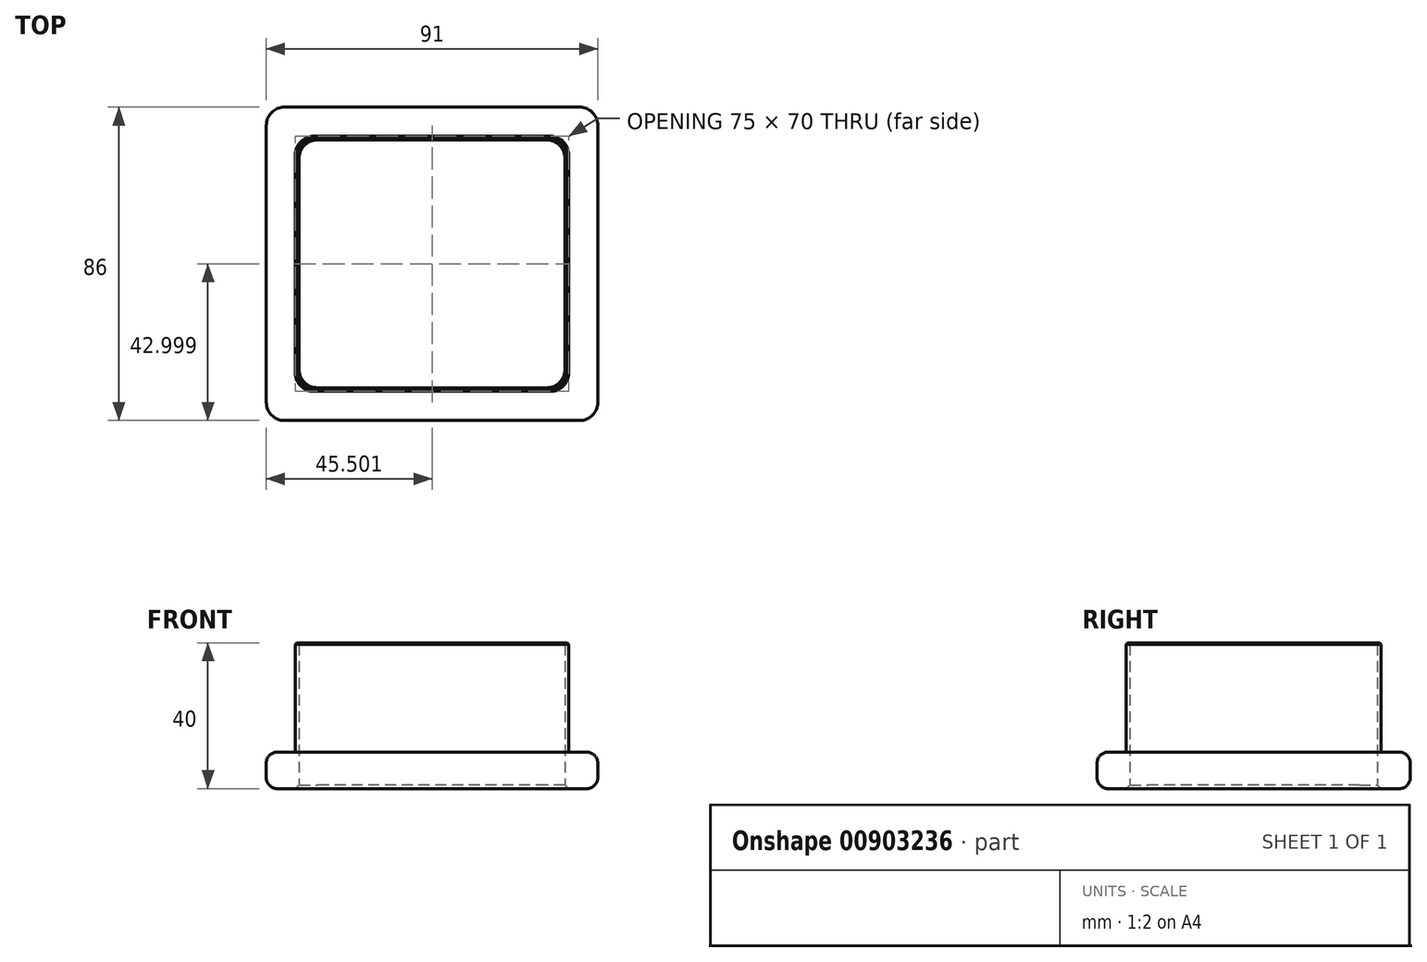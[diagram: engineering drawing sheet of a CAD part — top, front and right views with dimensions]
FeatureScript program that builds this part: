
annotation { "Feature Type Name" : "Feature", "Feature Type Description" : "" }
export const myFeature = defineFeature(function(context is Context, id is Id, definition is map)
    precondition{}
    {
        {
            var Q0;
            Q0=qCreatedBy(makeId("Top.planeOp"),FACE);
            var sketch = newSketch(context, id + "F0", { "sketchPlane" : qUnion([Q0])});
            skLineSegment(sketch, "E0.bottom", {"start": v(-97.4, 29.69) * mm, "end": v(-32.4, 29.69) * mm});
            skLineSegment(sketch, "E0.top", {"start": v(-97.4, -40.31) * mm, "end": v(-32.4, -40.31) * mm});
            skLineSegment(sketch, "E0.left", {"start": v(-102.4, 24.69) * mm, "end": v(-102.4, -35.31) * mm});
            skLineSegment(sketch, "E0.right", {"start": v(-27.4, 24.69) * mm, "end": v(-27.4, -35.31) * mm});
            skLineSegment(sketch, "E1.0", {"start": v(-101.4, 23.69) * mm, "end": v(-101.4, -34.31) * mm});
            skLineSegment(sketch, "E1.1", {"start": v(-96.4, 28.69) * mm, "end": v(-33.4, 28.69) * mm});
            skLineSegment(sketch, "E1.2", {"start": v(-28.4, 23.69) * mm, "end": v(-28.4, -34.31) * mm});
            skLineSegment(sketch, "E1.3", {"start": v(-96.4, -39.31) * mm, "end": v(-33.4, -39.31) * mm});
            skLineSegment(sketch, "E2.0", {"start": v(-105.4, 27.69) * mm, "end": v(-105.4, -38.31) * mm});
            skLineSegment(sketch, "E2.1", {"start": v(-100.4, 32.69) * mm, "end": v(-29.4, 32.69) * mm});
            skLineSegment(sketch, "E2.2", {"start": v(-24.4, 27.69) * mm, "end": v(-24.4, -38.31) * mm});
            skLineSegment(sketch, "E2.3", {"start": v(-100.4, -43.31) * mm, "end": v(-29.4, -43.31) * mm});
            skPoint(sketch, "E3.visualSharp", {"position": v(-101.4, 28.69) * mm});
            skArc(sketch, "E3.filletArc", {"start": v(-96.4, 28.69) * mm, "mid": v(-99.94, 27.22) * mm, "end": v(-101.4, 23.69) * mm});
            skPoint(sketch, "E4.visualSharp", {"position": v(-102.4, 29.69) * mm});
            skArc(sketch, "E4.filletArc", {"start": v(-97.4, 29.69) * mm, "mid": v(-100.94, 28.22) * mm, "end": v(-102.4, 24.69) * mm});
            skPoint(sketch, "E5.visualSharp", {"position": v(-27.4, 29.69) * mm});
            skArc(sketch, "E5.filletArc", {"start": v(-27.4, 24.69) * mm, "mid": v(-28.87, 28.22) * mm, "end": v(-32.4, 29.69) * mm});
            skPoint(sketch, "E6.visualSharp", {"position": v(-28.4, -39.31) * mm});
            skArc(sketch, "E6.filletArc", {"start": v(-33.4, -39.31) * mm, "mid": v(-29.87, -37.85) * mm, "end": v(-28.4, -34.31) * mm});
            skPoint(sketch, "E7.visualSharp", {"position": v(-27.4, -40.31) * mm});
            skArc(sketch, "E7.filletArc", {"start": v(-32.4, -40.31) * mm, "mid": v(-28.87, -38.85) * mm, "end": v(-27.4, -35.31) * mm});
            skPoint(sketch, "E8.visualSharp", {"position": v(-28.4, 28.69) * mm});
            skArc(sketch, "E8.filletArc", {"start": v(-28.4, 23.69) * mm, "mid": v(-29.87, 27.22) * mm, "end": v(-33.4, 28.69) * mm});
            skPoint(sketch, "E9.visualSharp", {"position": v(-101.4, -39.31) * mm});
            skArc(sketch, "E9.filletArc", {"start": v(-101.4, -34.31) * mm, "mid": v(-99.94, -37.85) * mm, "end": v(-96.4, -39.31) * mm});
            skPoint(sketch, "E10.visualSharp", {"position": v(-102.4, -40.31) * mm});
            skArc(sketch, "E10.filletArc", {"start": v(-102.4, -35.31) * mm, "mid": v(-100.94, -38.85) * mm, "end": v(-97.4, -40.31) * mm});
            skLineSegment(sketch, "E11.0", {"start": v(-105.4, 37.69) * mm, "end": v(-24.4, 37.69) * mm});
            skLineSegment(sketch, "E11.1", {"start": v(-110.4, 32.69) * mm, "end": v(-110.4, -43.31) * mm});
            skLineSegment(sketch, "E11.2", {"start": v(-105.4, -48.31) * mm, "end": v(-24.4, -48.31) * mm});
            skLineSegment(sketch, "E11.3", {"start": v(-19.4, 32.69) * mm, "end": v(-19.4, -43.31) * mm});
            skPoint(sketch, "E12.visualSharp", {"position": v(-105.4, 32.69) * mm});
            skArc(sketch, "E12.filletArc", {"start": v(-100.4, 32.69) * mm, "mid": v(-103.94, 31.22) * mm, "end": v(-105.4, 27.69) * mm});
            skPoint(sketch, "E13.visualSharp", {"position": v(-24.4, 32.69) * mm});
            skArc(sketch, "E13.filletArc", {"start": v(-24.4, 27.69) * mm, "mid": v(-25.87, 31.22) * mm, "end": v(-29.4, 32.69) * mm});
            skPoint(sketch, "E14.visualSharp", {"position": v(-24.4, -43.31) * mm});
            skArc(sketch, "E14.filletArc", {"start": v(-29.4, -43.31) * mm, "mid": v(-25.87, -41.85) * mm, "end": v(-24.4, -38.31) * mm});
            skPoint(sketch, "E15.visualSharp", {"position": v(-105.4, -43.31) * mm});
            skArc(sketch, "E15.filletArc", {"start": v(-105.4, -38.31) * mm, "mid": v(-103.94, -41.85) * mm, "end": v(-100.4, -43.31) * mm});
            skPoint(sketch, "E16.visualSharp", {"position": v(-110.4, -48.31) * mm});
            skArc(sketch, "E16.filletArc", {"start": v(-110.4, -43.31) * mm, "mid": v(-108.94, -46.85) * mm, "end": v(-105.4, -48.31) * mm});
            skPoint(sketch, "E17.visualSharp", {"position": v(-110.4, 37.69) * mm});
            skArc(sketch, "E17.filletArc", {"start": v(-105.4, 37.69) * mm, "mid": v(-108.94, 36.22) * mm, "end": v(-110.4, 32.69) * mm});
            skPoint(sketch, "E18.visualSharp", {"position": v(-19.4, 37.69) * mm});
            skArc(sketch, "E18.filletArc", {"start": v(-19.4, 32.69) * mm, "mid": v(-20.87, 36.22) * mm, "end": v(-24.4, 37.69) * mm});
            skPoint(sketch, "E19.visualSharp", {"position": v(-19.4, -48.31) * mm});
            skArc(sketch, "E19.filletArc", {"start": v(-24.4, -48.31) * mm, "mid": v(-20.87, -46.85) * mm, "end": v(-19.4, -43.31) * mm});
            skSolve(sketch);
        }
        {
            var Q0;
            Q0=makeQuery(id+"F0.imprint","IMPRINT",FACE,{"disambiguationData":[TD([[makeQuery(id+"F0.imprint","IMPRINT",EDGE,{"derivedFrom":sQuery(id+"F0.wireOp",EDGE,"E0.bottom")}),-1.0]])]});
            extrude(context, id + "F1", {"entities" : qUnion([Q0]), "depth" : 40 * mm, "offsetDistance" : 25 * mm});
        }
        {
            var Q0;
            Q0=makeQuery(id+"F0.imprint","IMPRINT",FACE,{"disambiguationData":[TD([[makeQuery(id+"F0.imprint","IMPRINT",EDGE,{"derivedFrom":sQuery(id+"F0.wireOp",EDGE,"E2.0")}),-1.0]])]});
            var Q1;
            Q1=makeQuery(id+"F0.imprint","IMPRINT",FACE,{"disambiguationData":[TD([[makeQuery(id+"F0.imprint","IMPRINT",EDGE,{"derivedFrom":sQuery(id+"F0.wireOp",EDGE,"E0.bottom")}),1.0]])]});
            extrude(context, id + "F2", {"entities" : qUnion([Q0, Q1]), "operationType" : NewBodyOperationType.ADD, "depth" : 10 * mm, "offsetDistance" : 25 * mm});
        }
        {
            var Q0;
            Q0=makeQuery(id+"F2.opExtrude","CAP_EDGE",EDGE,{"disambiguationData":[OSD([sQuery(id+"F0.wireOp",EDGE,"E0.top")])],"isStart":false});
            var Q1;
            Q1=makeQuery(id+"F2.opExtrude","CAP_EDGE",EDGE,{"disambiguationData":[OSD([sQuery(id+"F0.wireOp",EDGE,"E11.2")])],"isStart":false});
            var Q2;
            Q2=makeQuery(id+"F2.opExtrude","CAP_EDGE",EDGE,{"disambiguationData":[OSD([sQuery(id+"F0.wireOp",EDGE,"E11.2")])],"isStart":true});
            fillet(context, id + "F3", {"entities" : qUnion([Q0, Q1, Q2]), "radius" : 3 * mm, "tangentPropagation" : true, "allowEdgeOverflow" : false});
        }
        {
            var Q0;
            Q0=makeQuery(id+"F1.opExtrude","CAP_EDGE",EDGE,{"disambiguationData":[OSD([sQuery(id+"F0.wireOp",EDGE,"E0.top")])],"isStart":false});
            var Q1;
            Q1=makeQuery(id+"F1.opExtrude","CAP_EDGE",EDGE,{"disambiguationData":[OSD([sQuery(id+"F0.wireOp",EDGE,"E1.3")])],"isStart":false});
            chamfer(context, id + "F4", {"entities" : qUnion([Q0, Q1]), "width" : .4 * mm, "tangentPropagation" : true});
        }
        {
            var Q0;
            Q0=makeQuery(id+"F1.opExtrude","CAP_EDGE",EDGE,{"disambiguationData":[OSD([sQuery(id+"F0.wireOp",EDGE,"E1.0")])],"isStart":true});
            chamfer(context, id + "F5", {"entities" : qUnion([Q0]), "width" : 1 * mm, "tangentPropagation" : true});
        }
    });
